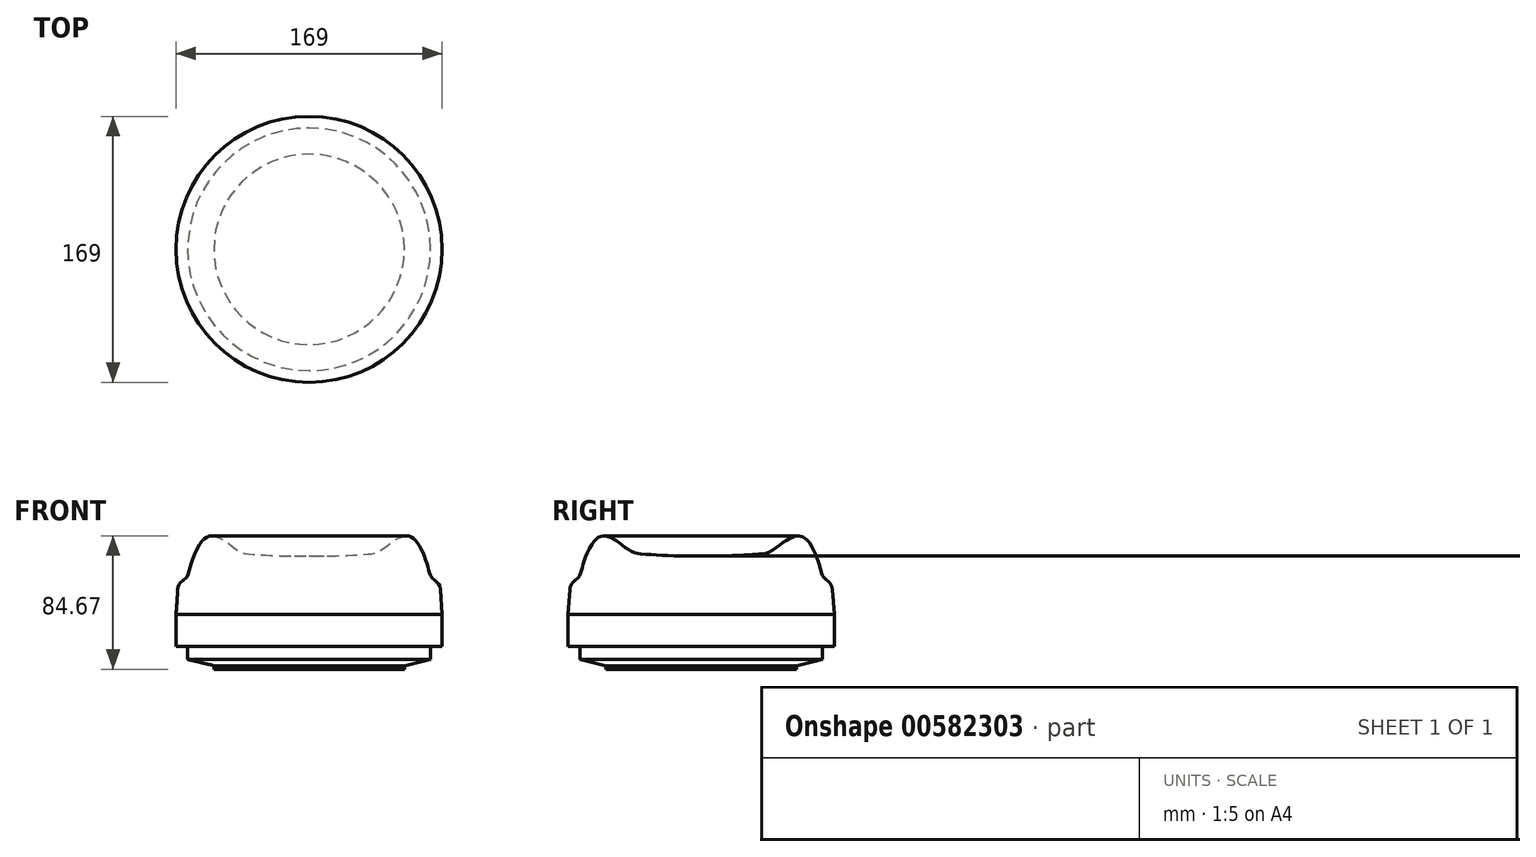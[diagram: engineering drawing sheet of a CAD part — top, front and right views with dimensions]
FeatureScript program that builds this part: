
annotation { "Feature Type Name" : "Feature", "Feature Type Description" : "" }
export const myFeature = defineFeature(function(context is Context, id is Id, definition is map)
    precondition{}
    {
        {
            var Q0;
            Q0=qCreatedBy(makeId("Front.planeOp"),FACE);
            var sketch = newSketch(context, id + "F0", { "sketchPlane" : qUnion([Q0])});
            skLineSegment(sketch, "E0", {"start": v(0, 0) * mm, "end": v(60.48, 0) * mm});
            skLineSegment(sketch, "E1", {"start": v(60.48, 0) * mm, "end": v(60.48, 2.23) * mm});
            skLineSegment(sketch, "E2", {"start": v(60.48, 2.23) * mm, "end": v(77.07, 6.2) * mm});
            skLineSegment(sketch, "E3", {"start": v(77.07, 6.2) * mm, "end": v(77.07, 14.39) * mm});
            skLineSegment(sketch, "E4", {"start": v(77.07, 14.39) * mm, "end": v(84.5, 14.39) * mm});
            skLineSegment(sketch, "E5", {"start": v(84.5, 34.72) * mm, "end": v(83.38, 50.63) * mm});
            skLineSegment(sketch, "E6", {"start": v(84.5, 14.39) * mm, "end": v(84.5, 34.72) * mm});
            skLineSegment(sketch, "E7", {"start": v(0, 0) * mm, "end": v(0, 72) * mm});
            skFitSpline(sketch, "E8", {"points": [v(0, 72) * mm, v(16.7, 72) * mm, v(34.78, 72.95) * mm, v(43.64, 74.49) * mm, v(52.85, 80.98) * mm, v(57.34, 83.46) * mm, v(62.54, 84.65) * mm, v(68.45, 80.75) * mm, v(74.82, 67.04) * mm, v(77.54, 58.66) * mm, v(80.14, 56.3) * mm, v(83.38, 50.63) * mm], "startDerivative": vector(130.75, -2.35) * mm, "endDerivative": vector(7.83, -111.8) * mm});
            skSolve(sketch);
        }
        {
            var Q0;
            Q0=makeQuery(id+"F0.imprint","IMPRINT",FACE,{"disambiguationData":[TD([[makeQuery(id+"F0.imprint","IMPRINT",EDGE,{"derivedFrom":sQuery(id+"F0.wireOp",EDGE,"E0")}),1.0]])]});
            var Q1;
            Q1=sQuery(id+"F0.wireOp",EDGE,"E7");
            revolve(context, id + "F1", {"entities" : qUnion([Q0]), "axis" : qUnion([Q1]), "revolveType" : RevolveType.FULL});
        }
    });
